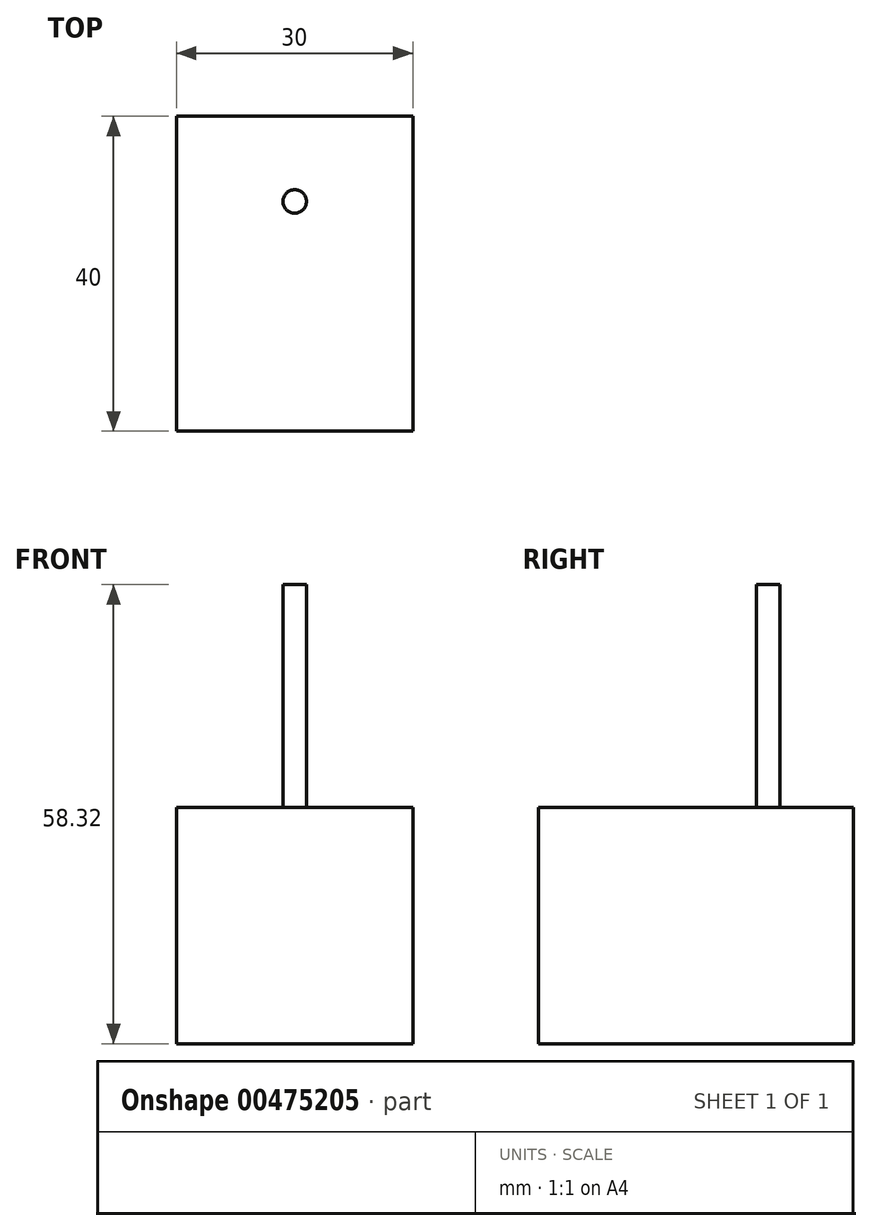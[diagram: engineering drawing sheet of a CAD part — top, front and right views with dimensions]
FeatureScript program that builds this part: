
annotation { "Feature Type Name" : "Feature", "Feature Type Description" : "" }
export const myFeature = defineFeature(function(context is Context, id is Id, definition is map)
    precondition{}
    {
        {
            var Q0;
            Q0=qCreatedBy(makeId("Top.planeOp"),FACE);
            var sketch = newSketch(context, id + "F0", { "sketchPlane" : qUnion([Q0])});
            skLineSegment(sketch, "E0.bottom", {"start": v(0, 0) * mm, "end": v(30, 0) * mm});
            skLineSegment(sketch, "E0.top", {"start": v(0, -40) * mm, "end": v(30, -40) * mm});
            skLineSegment(sketch, "E0.left", {"start": v(0, 0) * mm, "end": v(0, -40) * mm});
            skLineSegment(sketch, "E0.right", {"start": v(30, 0) * mm, "end": v(30, -40) * mm});
            skSolve(sketch);
        }
        {
            var Q0;
            Q0=makeQuery(id+"F0.imprint","IMPRINT",FACE,{"disambiguationData":[TD([[makeQuery(id+"F0.imprint","IMPRINT",EDGE,{"derivedFrom":sQuery(id+"F0.wireOp",EDGE,"E0.bottom")}),-1.0]])]});
            extrude(context, id + "F1", {"entities" : qUnion([Q0]), "oppositeDirection" : true, "depth" : 30 * mm});
        }
        {
            var Q0;
            Q0=makeQuery(id+"F1.opExtrude","CAP_FACE",FACE,{"disambiguationData":[OSD([sQuery(id+"F0.wireOp",EDGE,"E0.bottom"),sQuery(id+"F0.wireOp",EDGE,"E0.top"),sQuery(id+"F0.wireOp",EDGE,"E0.left"),sQuery(id+"F0.wireOp",EDGE,"E0.right")])],"isStart":false});
            var sketch = newSketch(context, id + "F2", { "sketchPlane" : qUnion([Q0])});
            skPoint(sketch, "E1.endSnap0", {"position": v(15, 40) * mm});
            skCircle(sketch, "E2", {"center": v(15, 10.83) * mm, "radius": 1.5 * mm});
            skSolve(sketch);
        }
        {
            var Q0;
            Q0 = qSketchRegion(id + "F2", true);
            extrude(context, id + "F3", {"entities" : qUnion([Q0]), "operationType" : NewBodyOperationType.ADD, "endBound" : BoundingType.THROUGH_ALL, "oppositeDirection" : true, "depth" : 25 * mm});
        }
    });
